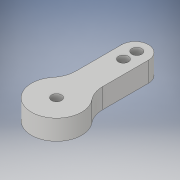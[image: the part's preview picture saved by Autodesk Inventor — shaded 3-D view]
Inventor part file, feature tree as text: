
AUTODESK INVENTOR PART (.ipt)
format: ipt  version: 2019 (Build 230136000, 136)  size: 142,848 bytes
history: native  units: mm
features: extrude x3, sketch x3, fillet x1
ambient origin geometry x8: Origin, YZ Plane, XZ Plane, XY Plane, X Axis, Y Axis, Z Axis, Center Point
bodies: Solid1 (feature_tree)
feature tree (7):
  extrude  "Extrusion1"  Depth=35.0mm
  fillet  "Fillet1"  [1 undecoded]
  extrude  "Extrusion2"  Depth=6.0mm TaperAngle=0.0deg
  extrude  "Extrusion3"  Depth=3.0mm
  sketch  "Sketch1"  dims[d0=15.0mm d1=35.0mm d2=0.0mm]
  sketch  "Sketch2"  dims[d3=4.0mm d4=6.0mm d5=0.0mm]
  sketch  "Sketch3"  dims[d6=8.0mm d8=3.5mm d9=3.0mm d10=4.0mm d11=3.0mm d12=3.0mm d13=6.0mm d14=0.0mm d15=5.6mm d16=3.0mm d17=0.0mm]
note: 1 required parameter value undecoded (feature->parameter linkage not recoverable at this tier; creation-order binding heuristic only, values carry confidence <= 0.55)
